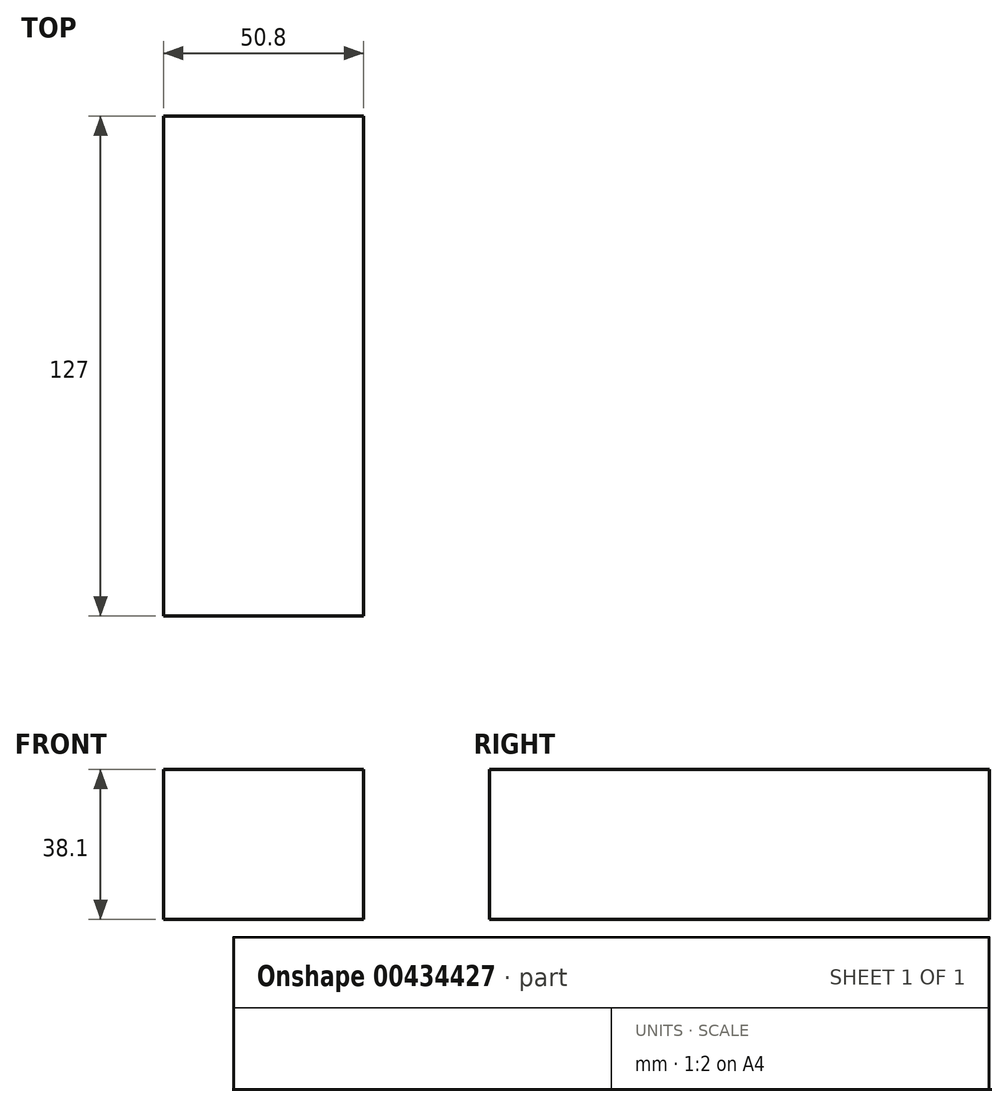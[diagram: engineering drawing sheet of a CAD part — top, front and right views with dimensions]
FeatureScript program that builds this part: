
annotation { "Feature Type Name" : "Feature", "Feature Type Description" : "" }
export const myFeature = defineFeature(function(context is Context, id is Id, definition is map)
    precondition{}
    {
        {
            var Q0;
            Q0=qCreatedBy(makeId("Front.planeOp"),FACE);
            var sketch = newSketch(context, id + "F0", { "sketchPlane" : qUnion([Q0])});
            skLineSegment(sketch, "E0.bottom", {"start": v(-55.24, 18.73) * mm, "end": v(-4.44, 18.73) * mm});
            skLineSegment(sketch, "E0.top", {"start": v(-55.24, -19.37) * mm, "end": v(-4.44, -19.37) * mm});
            skLineSegment(sketch, "E0.left", {"start": v(-55.24, 18.73) * mm, "end": v(-55.24, -19.37) * mm});
            skLineSegment(sketch, "E0.right", {"start": v(-4.44, 18.73) * mm, "end": v(-4.44, -19.37) * mm});
            skSolve(sketch);
        }
        {
            var Q0;
            Q0=makeQuery(id+"F0.imprint","IMPRINT",FACE,{"disambiguationData":[TD([[makeQuery(id+"F0.imprint","IMPRINT",EDGE,{"derivedFrom":sQuery(id+"F0.wireOp",EDGE,"E0.bottom")}),-1.0]])]});
            extrude(context, id + "F1", {"entities" : qUnion([Q0]), "depth" : 127 * mm});
        }
    });
